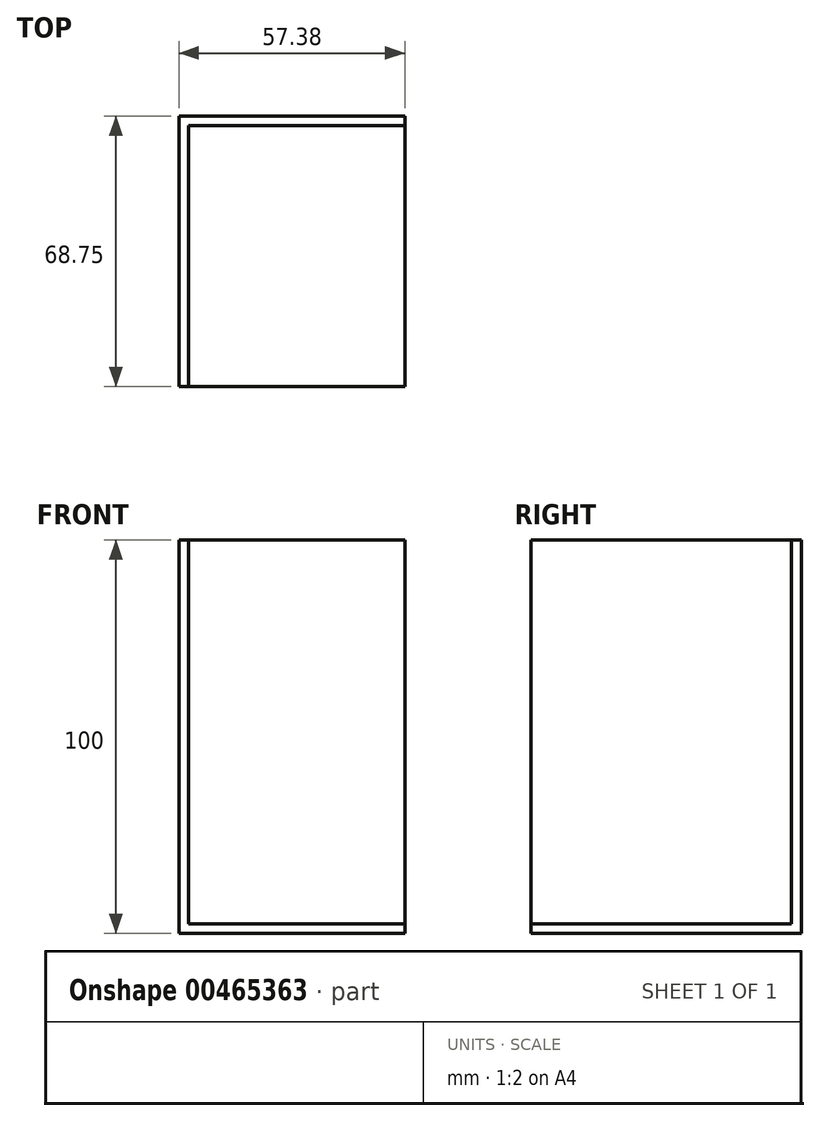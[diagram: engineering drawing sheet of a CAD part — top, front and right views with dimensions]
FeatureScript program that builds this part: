
annotation { "Feature Type Name" : "Feature", "Feature Type Description" : "" }
export const myFeature = defineFeature(function(context is Context, id is Id, definition is map)
    precondition{}
    {
        {
            var Q0;
            Q0=qCreatedBy(makeId("Top.planeOp"),FACE);
            var sketch = newSketch(context, id + "F0", { "sketchPlane" : qUnion([Q0])});
            skLineSegment(sketch, "E0.bottom", {"start": v(-27.92, 31.33) * mm, "end": v(29.46, 31.33) * mm});
            skLineSegment(sketch, "E0.top", {"start": v(-27.92, -37.42) * mm, "end": v(29.46, -37.42) * mm});
            skLineSegment(sketch, "E0.left", {"start": v(-27.92, 31.33) * mm, "end": v(-27.92, -37.42) * mm});
            skLineSegment(sketch, "E0.right", {"start": v(29.46, 31.33) * mm, "end": v(29.46, -37.42) * mm});
            skSolve(sketch);
        }
        {
            var Q0;
            Q0=makeQuery(id+"F0.imprint","IMPRINT",FACE,{"disambiguationData":[TD([[makeQuery(id+"F0.imprint","IMPRINT",EDGE,{"derivedFrom":sQuery(id+"F0.wireOp",EDGE,"E0.bottom")}),-1.0]])]});
            extrude(context, id + "F1", {"entities" : qUnion([Q0]), "depth" : 100 * mm});
        }
        {
            var Q0;
            Q0=makeQuery(id+"F1.opExtrude","CAP_FACE",FACE,{"disambiguationData":[OSD([sQuery(id+"F0.wireOp",EDGE,"E0.bottom"),sQuery(id+"F0.wireOp",EDGE,"E0.top"),sQuery(id+"F0.wireOp",EDGE,"E0.left"),sQuery(id+"F0.wireOp",EDGE,"E0.right")])],"isStart":false});
            var Q1;
            Q1=makeQuery(id+"F1.opExtrude","SWEPT_FACE",FACE,{"disambiguationData":[OSD([sQuery(id+"F0.wireOp",EDGE,"E0.right")])]});
            var Q2;
            Q2=makeQuery(id+"F1.opExtrude","SWEPT_FACE",FACE,{"disambiguationData":[OSD([sQuery(id+"F0.wireOp",EDGE,"E0.top")])]});
            shell(context, id + "F2", {"entities" : qUnion([Q0, Q1, Q2]), "thickness" : 2.5 * mm});
        }
    });
